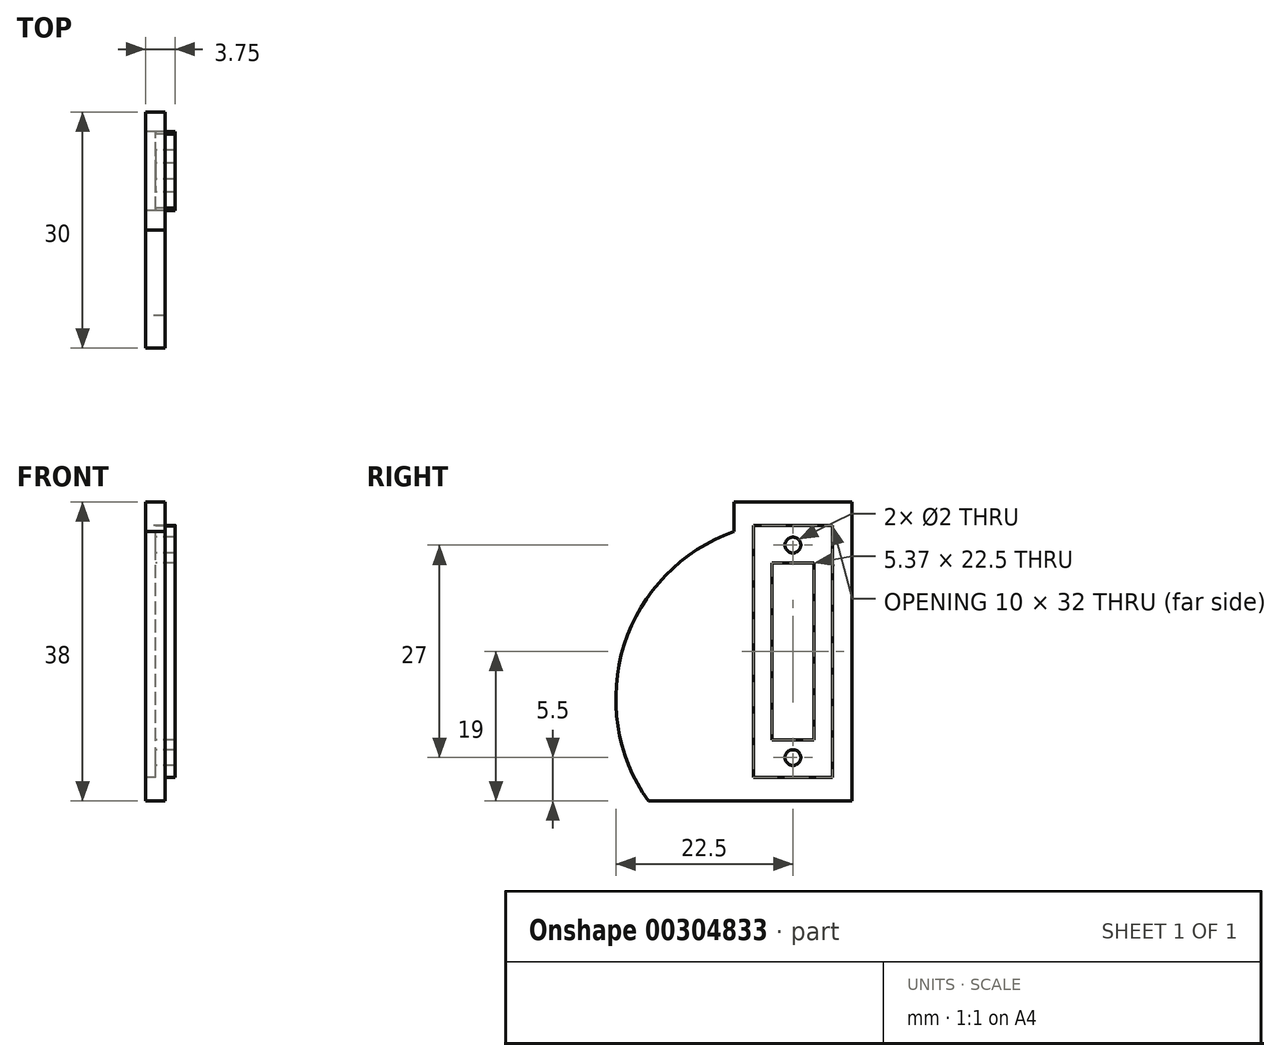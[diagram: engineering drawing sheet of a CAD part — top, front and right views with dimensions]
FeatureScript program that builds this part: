
annotation { "Feature Type Name" : "Feature", "Feature Type Description" : "" }
export const myFeature = defineFeature(function(context is Context, id is Id, definition is map)
    precondition{}
    {
        {
            var Q0;
            Q0=qCreatedBy(makeId("Right.planeOp"),FACE);
            var sketch = newSketch(context, id + "F0", { "sketchPlane" : qUnion([Q0])});
            skLineSegment(sketch, "E0.bottom", {"start": v(7.5, -19) * mm, "end": v(-7.5, -19) * mm});
            skLineSegment(sketch, "E0.top", {"start": v(7.5, 19) * mm, "end": v(-7.5, 19) * mm});
            skLineSegment(sketch, "E0.left", {"start": v(7.5, -19) * mm, "end": v(7.5, 19) * mm});
            skLineSegment(sketch, "E0.right", {"start": v(-7.5, -19) * mm, "end": v(-7.5, 19) * mm});
            skPoint(sketch, "E0.middle", {"position": v(0, 0) * mm});
            skLineSegment(sketch, "E1.bottom", {"start": v(5, -11.25) * mm, "end": v(-5, -11.25) * mm});
            skLineSegment(sketch, "E1.top", {"start": v(5, 11.25) * mm, "end": v(-5, 11.25) * mm});
            skLineSegment(sketch, "E1.left", {"start": v(5, -11.25) * mm, "end": v(5, 11.25) * mm});
            skLineSegment(sketch, "E1.right", {"start": v(-5, -11.25) * mm, "end": v(-5, 11.25) * mm});
            skLineSegment(sketch, "E2.bottom", {"start": v(2.69, -13.5) * mm, "end": v(-2.69, -13.5) * mm});
            skLineSegment(sketch, "E2.top", {"start": v(2.69, 13.5) * mm, "end": v(-2.69, 13.5) * mm});
            skLineSegment(sketch, "E2.left", {"start": v(2.69, -13.5) * mm, "end": v(2.69, 13.5) * mm});
            skLineSegment(sketch, "E2.right", {"start": v(-2.69, -13.5) * mm, "end": v(-2.69, 13.5) * mm});
            skCircle(sketch, "E3", {"center": v(0, 13.5) * mm, "radius": 1 * mm});
            skCircle(sketch, "E4", {"center": v(0, -13.5) * mm, "radius": 1 * mm});
            skPoint(sketch, "E5.endSnap0", {"position": v(0, 11.25) * mm});
            skLineSegment(sketch, "E6.bottom", {"start": v(-5, -16) * mm, "end": v(5, -16) * mm});
            skLineSegment(sketch, "E6.top", {"start": v(-5, 16) * mm, "end": v(5, 16) * mm});
            skLineSegment(sketch, "E6.left", {"start": v(-5, -16) * mm, "end": v(-5, 16) * mm});
            skLineSegment(sketch, "E6.right", {"start": v(5, -16) * mm, "end": v(5, 16) * mm});
            skLineSegment(sketch, "E7", {"start": v(0, 16) * mm, "end": v(0, -6) * mm});
            skPoint(sketch, "E7.endSnap0", {"position": v(0, -11.25) * mm});
            skCircle(sketch, "E8", {"center": v(0, -6) * mm, "radius": 22.5 * mm});
            skLineSegment(sketch, "E9.bottom", {"start": v(-50, -37.5) * mm, "end": v(50, -37.5) * mm});
            skLineSegment(sketch, "E9.top", {"start": v(-50, 37.5) * mm, "end": v(50, 37.5) * mm});
            skLineSegment(sketch, "E9.left", {"start": v(-50, -37.5) * mm, "end": v(-50, 37.5) * mm});
            skLineSegment(sketch, "E9.right", {"start": v(50, -37.5) * mm, "end": v(50, 37.5) * mm});
            skLineSegment(sketch, "E10.top", {"start": v(0, -19) * mm, "end": v(-50, -19) * mm});
            skLineSegment(sketch, "E10.left", {"start": v(0, 16) * mm, "end": v(0, -19) * mm});
            skLineSegment(sketch, "E10.right", {"start": v(-50, 16) * mm, "end": v(-50, -19) * mm});
            skLineSegment(sketch, "E11", {"start": v(-7.5, 19) * mm, "end": v(-50, 19) * mm});
            skSolve(sketch);
        }
        {
            var Q0;
            {var subQ3=sQuery(id+"F0.wireOp",EDGE,"E1.top");var subQ5=sQuery(id+"F0.wireOp",EDGE,"E6.right");var subQ6=makeQuery(id+"F0.imprint","INTERSECT",VERTEX,{"derivedFrom":[subQ3,subQ5]});Q0=makeQuery(id+"F0.imprint","IMPRINT",FACE,{"disambiguationData":[TD([[makeQuery(id+"F0.imprint","IMPRINT",EDGE,{"disambiguationData":[TD([[subQ6,-1.0]])],"derivedFrom":subQ3}),-1.0]])]});}
            var Q1;
            {var subQ6=sQuery(id+"F0.wireOp",EDGE,"E6.left");var subQ12=sQuery(id+"F0.wireOp",EDGE,"E1.top");var subQ15=makeQuery(id+"F0.imprint","INTERSECT",VERTEX,{"derivedFrom":[subQ12,subQ6]});Q1=makeQuery(id+"F0.imprint","IMPRINT",FACE,{"disambiguationData":[TD([[makeQuery(id+"F0.imprint","IMPRINT",EDGE,{"disambiguationData":[TD([[subQ15,1.0]])],"derivedFrom":subQ12}),-1.0]])]});}
            var Q2;
            {var subQ0=sQuery(id+"F0.wireOp",EDGE,"E2.left");var subQ3=sQuery(id+"F0.wireOp",EDGE,"E1.top");var subQ4=makeQuery(id+"F0.imprint","INTERSECT",VERTEX,{"derivedFrom":[subQ3,subQ0]});Q2=makeQuery(id+"F0.imprint","IMPRINT",FACE,{"disambiguationData":[TD([[makeQuery(id+"F0.imprint","IMPRINT",EDGE,{"disambiguationData":[TD([[subQ4,-1.0]])],"derivedFrom":subQ3}),-1.0]])]});}
            var Q3;
            {var subQ3=sQuery(id+"F0.wireOp",EDGE,"E10.left");var subQ7=sQuery(id+"F0.wireOp",EDGE,"E1.top");var subQ9=makeQuery(id+"F0.imprint","INTERSECT",VERTEX,{"derivedFrom":[subQ7,subQ3]});Q3=makeQuery(id+"F0.imprint","IMPRINT",FACE,{"disambiguationData":[TD([[makeQuery(id+"F0.imprint","IMPRINT",EDGE,{"disambiguationData":[TD([[subQ9,-1.0]])],"derivedFrom":subQ7}),-1.0]])]});}
            var Q4;
            {var subQ3=sQuery(id+"F0.wireOp",EDGE,"E1.bottom");var subQ7=sQuery(id+"F0.wireOp",EDGE,"E10.left");var subQ9=makeQuery(id+"F0.imprint","INTERSECT",VERTEX,{"derivedFrom":[subQ3,subQ7]});Q4=makeQuery(id+"F0.imprint","IMPRINT",FACE,{"disambiguationData":[TD([[makeQuery(id+"F0.imprint","IMPRINT",EDGE,{"disambiguationData":[TD([[subQ9,-1.0]])],"derivedFrom":subQ3}),1.0]])]});}
            var Q5;
            {var subQ0=sQuery(id+"F0.wireOp",EDGE,"E2.left");var subQ7=sQuery(id+"F0.wireOp",EDGE,"E1.bottom");var subQ8=makeQuery(id+"F0.imprint","INTERSECT",VERTEX,{"derivedFrom":[subQ7,subQ0]});Q5=makeQuery(id+"F0.imprint","IMPRINT",FACE,{"disambiguationData":[TD([[makeQuery(id+"F0.imprint","IMPRINT",EDGE,{"disambiguationData":[TD([[subQ8,-1.0]])],"derivedFrom":subQ7}),1.0]])]});}
            var Q6;
            {var subQ7=sQuery(id+"F0.wireOp",EDGE,"E1.bottom");var subQ9=sQuery(id+"F0.wireOp",EDGE,"E6.right");var subQ10=makeQuery(id+"F0.imprint","INTERSECT",VERTEX,{"derivedFrom":[subQ7,subQ9]});Q6=makeQuery(id+"F0.imprint","IMPRINT",FACE,{"disambiguationData":[TD([[makeQuery(id+"F0.imprint","IMPRINT",EDGE,{"disambiguationData":[TD([[subQ10,-1.0]])],"derivedFrom":subQ7}),1.0]])]});}
            var Q7;
            {var subQ3=sQuery(id+"F0.wireOp",EDGE,"E1.bottom");var subQ5=sQuery(id+"F0.wireOp",EDGE,"E6.left");var subQ13=makeQuery(id+"F0.imprint","INTERSECT",VERTEX,{"derivedFrom":[subQ3,subQ5]});Q7=makeQuery(id+"F0.imprint","IMPRINT",FACE,{"disambiguationData":[TD([[makeQuery(id+"F0.imprint","IMPRINT",EDGE,{"disambiguationData":[TD([[subQ13,1.0]])],"derivedFrom":subQ3}),1.0]])]});}
            var Q8;
            {var subQ0=sQuery(id+"F0.wireOp",EDGE,"E6.left");var subQ1=sQuery(id+"F0.wireOp",EDGE,"E1.bottom");var subQ2=makeQuery(id+"F0.imprint","INTERSECT",VERTEX,{"derivedFrom":[subQ1,subQ0]});Q8=makeQuery(id+"F0.imprint","IMPRINT",FACE,{"disambiguationData":[TD([[makeQuery(id+"F0.imprint","IMPRINT",EDGE,{"disambiguationData":[TD([[subQ2,1.0]])],"derivedFrom":subQ1}),-1.0]])]});}
            var Q9;
            {var subQ0=sQuery(id+"F0.wireOp",EDGE,"E6.right");var subQ1=sQuery(id+"F0.wireOp",EDGE,"E1.bottom");var subQ2=makeQuery(id+"F0.imprint","INTERSECT",VERTEX,{"derivedFrom":[subQ1,subQ0]});Q9=makeQuery(id+"F0.imprint","IMPRINT",FACE,{"disambiguationData":[TD([[makeQuery(id+"F0.imprint","IMPRINT",EDGE,{"disambiguationData":[TD([[subQ2,-1.0]])],"derivedFrom":subQ1}),-1.0]])]});}
            extrude(context, id + "F1", {"entities" : qUnion([Q0, Q1, Q2, Q3, Q4, Q5, Q6, Q7, Q8, Q9]), "depth" : 2.5 * mm});
        }
        {
            var Q0;
            {var subQ0=sQuery(id+"F0.wireOp",EDGE,"E10.right");Q0=makeQuery(id+"F0.imprint","IMPRINT",FACE,{"disambiguationData":[TD([[makeQuery(id+"F0.imprint","IMPRINT",EDGE,{"derivedFrom":subQ0}),1.0]])]});}
            var Q1;
            {var subQ0=sQuery(id+"F0.wireOp",EDGE,"E10.top");var subQ1=sQuery(id+"F0.wireOp",EDGE,"E0.right");var subQ2=makeQuery(id+"F0.imprint","INTERSECT",VERTEX,{"derivedFrom":[subQ1,subQ0]});Q1=makeQuery(id+"F0.imprint","IMPRINT",FACE,{"disambiguationData":[TD([[makeQuery(id+"F0.imprint","IMPRINT",EDGE,{"disambiguationData":[TD([[subQ2,-1.0]])],"derivedFrom":subQ1}),1.0]])]});}
            var Q2;
            {var subQ6=sQuery(id+"F0.wireOp",EDGE,"E0.right");var subQ11=sQuery(id+"F0.wireOp",EDGE,"E10.top");var subQ12=makeQuery(id+"F0.imprint","INTERSECT",VERTEX,{"derivedFrom":[subQ6,subQ11]});Q2=makeQuery(id+"F0.imprint","IMPRINT",FACE,{"disambiguationData":[TD([[makeQuery(id+"F0.imprint","IMPRINT",EDGE,{"disambiguationData":[TD([[subQ12,-1.0]])],"derivedFrom":subQ6}),-1.0]])]});}
            var Q3;
            {var subQ0=sQuery(id+"F0.wireOp",EDGE,"E8");var subQ1=sQuery(id+"F0.wireOp",EDGE,"E0.right");var subQ2=makeQuery(id+"F0.imprint","INTERSECT",VERTEX,{"derivedFrom":[subQ1,subQ0]});Q3=makeQuery(id+"F0.imprint","IMPRINT",FACE,{"disambiguationData":[TD([[makeQuery(id+"F0.imprint","IMPRINT",EDGE,{"disambiguationData":[TD([[subQ2,-1.0]])],"derivedFrom":subQ1}),-1.0]])]});}
            var Q4;
            {var subQ9=sQuery(id+"F0.wireOp",EDGE,"E0.top");Q4=makeQuery(id+"F0.imprint","IMPRINT",FACE,{"disambiguationData":[TD([[makeQuery(id+"F0.imprint","IMPRINT",EDGE,{"derivedFrom":subQ9}),1.0]])]});}
            var Q5;
            {var subQ9=sQuery(id+"F0.wireOp",EDGE,"E0.bottom");Q5=makeQuery(id+"F0.imprint","IMPRINT",FACE,{"disambiguationData":[TD([[makeQuery(id+"F0.imprint","IMPRINT",EDGE,{"derivedFrom":subQ9}),-1.0]])]});}
            var Q6;
            {var subQ1=sQuery(id+"F0.wireOp",EDGE,"E6.top");var subQ3=sQuery(id+"F0.wireOp",EDGE,"E8");var subQ4=makeQuery(id+"F0.imprint","INTERSECT",VERTEX,{"derivedFrom":[subQ1,subQ3]});Q6=makeQuery(id+"F0.imprint","IMPRINT",FACE,{"disambiguationData":[TD([[makeQuery(id+"F0.imprint","IMPRINT",EDGE,{"disambiguationData":[TD([[subQ4,-1.0]])],"derivedFrom":subQ3}),1.0]])]});}
            extrude(context, id + "F2", {"entities" : qUnion([Q0, Q1, Q2, Q3, Q4, Q5, Q6]), "operationType" : NewBodyOperationType.ADD, "endBound" : BoundingType.SYMMETRIC, "depth" : 2.5 * mm});
        }
    });
